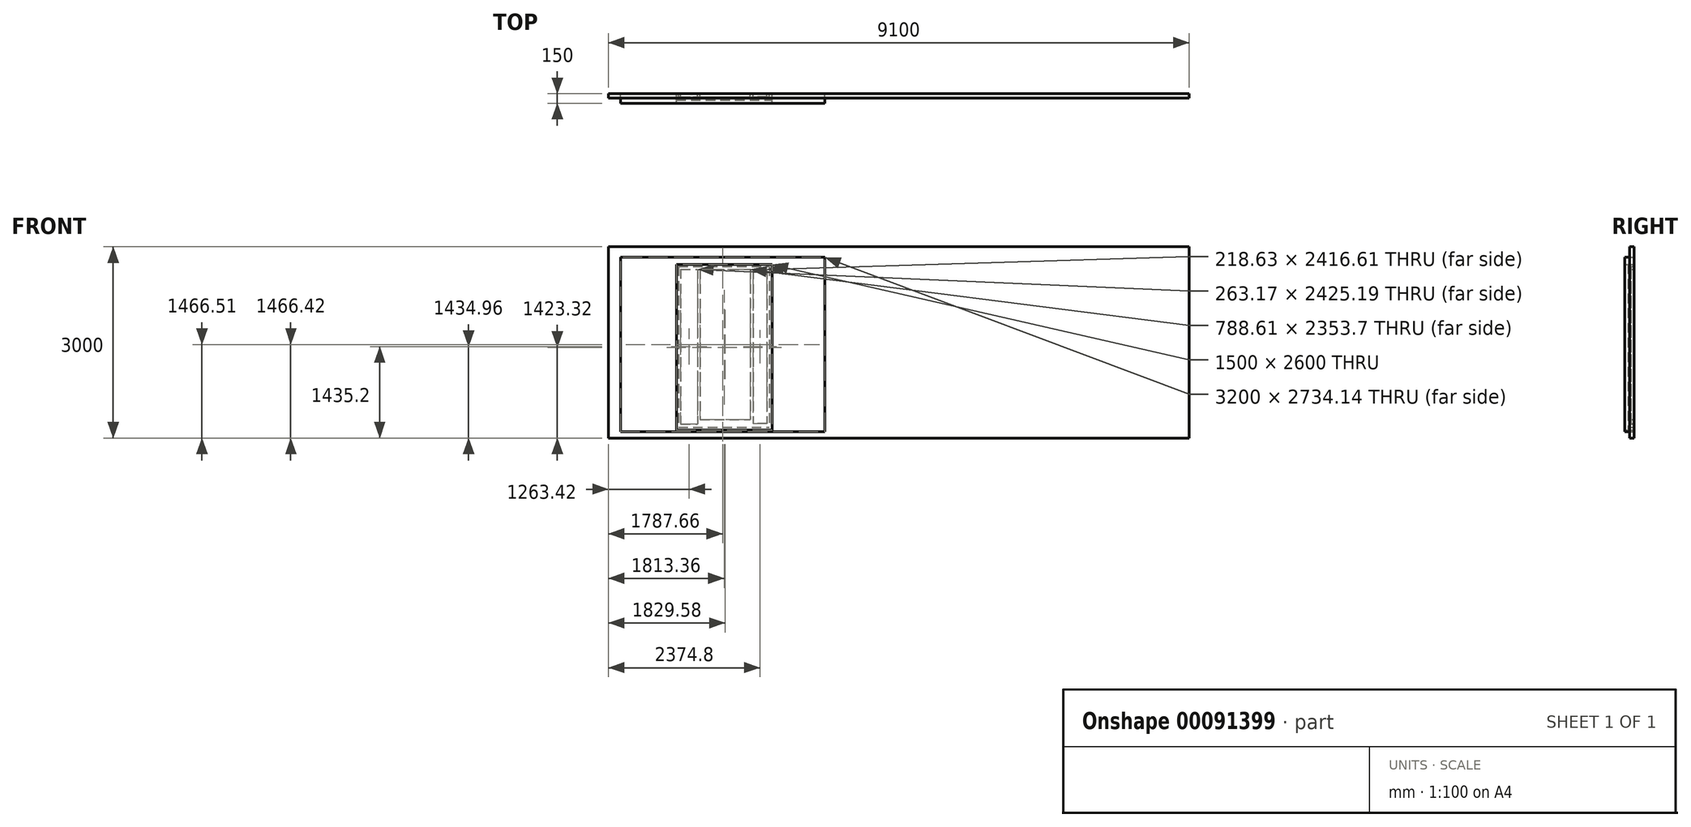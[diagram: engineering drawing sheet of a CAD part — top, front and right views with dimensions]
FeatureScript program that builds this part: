
annotation { "Feature Type Name" : "Feature", "Feature Type Description" : "" }
export const myFeature = defineFeature(function(context is Context, id is Id, definition is map)
    precondition{}
    {
        {
            var Q0;
            Q0=qCreatedBy(makeId("Front.planeOp"),FACE);
            var sketch = newSketch(context, id + "F0", { "sketchPlane" : qUnion([Q0])});
            skLineSegment(sketch, "E0.bottom", {"start": v(-2377.1, 2154.8) * mm, "end": v(6722.9, 2154.8) * mm});
            skLineSegment(sketch, "E0.top", {"start": v(-2377.1, -845.2) * mm, "end": v(6722.9, -845.2) * mm});
            skLineSegment(sketch, "E0.left", {"start": v(-2377.1, 2154.8) * mm, "end": v(-2377.1, -845.2) * mm});
            skLineSegment(sketch, "E0.right", {"start": v(6722.9, 2154.8) * mm, "end": v(6722.9, -845.2) * mm});
            skLineSegment(sketch, "E1.bottom", {"start": v(-2189.44, -745.77) * mm, "end": v(1010.56, -745.77) * mm});
            skLineSegment(sketch, "E1.top", {"start": v(-2189.44, 1988.37) * mm, "end": v(1010.56, 1988.37) * mm});
            skLineSegment(sketch, "E1.left", {"start": v(-2189.44, -745.77) * mm, "end": v(-2189.44, 1988.37) * mm});
            skLineSegment(sketch, "E1.right", {"start": v(1010.56, -745.77) * mm, "end": v(1010.56, 1988.37) * mm});
            skLineSegment(sketch, "E2.bottom", {"start": v(-1313.74, 1878.1) * mm, "end": v(186.26, 1878.1) * mm});
            skLineSegment(sketch, "E2.top", {"start": v(-1313.74, -721.9) * mm, "end": v(186.26, -721.9) * mm});
            skLineSegment(sketch, "E2.left", {"start": v(-1313.74, 1878.1) * mm, "end": v(-1313.74, -721.9) * mm});
            skLineSegment(sketch, "E2.right", {"start": v(186.26, 1878.1) * mm, "end": v(186.26, -721.9) * mm});
            skSolve(sketch);
        }
        {
            var Q0;
            Q0=makeQuery(id+"F0.imprint","IMPRINT",FACE,{"disambiguationData":[TD([[makeQuery(id+"F0.imprint","IMPRINT",EDGE,{"derivedFrom":sQuery(id+"F0.wireOp",EDGE,"E0.bottom")}),-1.0]])]});
            extrude(context, id + "F1", {"entities" : qUnion([Q0]), "depth" : 70 * mm});
        }
        {
            var Q0;
            Q0=makeQuery(id+"F0.imprint","IMPRINT",FACE,{"disambiguationData":[TD([[makeQuery(id+"F0.imprint","IMPRINT",EDGE,{"derivedFrom":sQuery(id+"F0.wireOp",EDGE,"E1.bottom")}),1.0]])]});
            extrude(context, id + "F2", {"entities" : qUnion([Q0]), "depth" : 150 * mm});
        }
        {
            var Q0;
            Q0=makeQuery(id+"F0.imprint","IMPRINT",FACE,{"disambiguationData":[TD([[makeQuery(id+"F0.imprint","IMPRINT",EDGE,{"derivedFrom":sQuery(id+"F0.wireOp",EDGE,"E2.bottom")}),-1.0]])]});
            extrude(context, id + "F3", {"entities" : qUnion([Q0]), "depth" : 100 * mm});
        }
        {
            var Q0;
            Q0=qCreatedBy(makeId("Front.planeOp"),FACE);
            var sketch = newSketch(context, id + "F4", { "sketchPlane" : qUnion([Q0])});
            skLineSegment(sketch, "E3.bottom", {"start": v(-1281.54, 1846.59) * mm, "end": v(144.03, 1846.59) * mm});
            skLineSegment(sketch, "E3.top", {"start": v(-1281.54, -676.97) * mm, "end": v(144.03, -676.97) * mm});
            skLineSegment(sketch, "E3.left", {"start": v(-1281.54, 1846.59) * mm, "end": v(-1281.54, -676.97) * mm});
            skLineSegment(sketch, "E3.right", {"start": v(144.03, 1846.59) * mm, "end": v(144.03, -676.97) * mm});
            skLineSegment(sketch, "E4.bottom", {"start": v(-941.83, 1798.06) * mm, "end": v(-153.22, 1798.06) * mm});
            skLineSegment(sketch, "E4.top", {"start": v(-941.83, -555.64) * mm, "end": v(-153.22, -555.64) * mm});
            skLineSegment(sketch, "E4.left", {"start": v(-941.83, 1798.06) * mm, "end": v(-941.83, -555.64) * mm});
            skLineSegment(sketch, "E4.right", {"start": v(-153.22, 1798.06) * mm, "end": v(-153.22, -555.64) * mm});
            skLineSegment(sketch, "E5.bottom", {"start": v(-1245.26, 1802.59) * mm, "end": v(-982.1, 1802.59) * mm});
            skLineSegment(sketch, "E5.top", {"start": v(-1245.26, -622.6) * mm, "end": v(-982.1, -622.6) * mm});
            skLineSegment(sketch, "E5.left", {"start": v(-1245.26, 1802.59) * mm, "end": v(-1245.26, -622.6) * mm});
            skLineSegment(sketch, "E5.right", {"start": v(-982.1, 1802.59) * mm, "end": v(-982.1, -622.6) * mm});
            skLineSegment(sketch, "E6.bottom", {"start": v(107.01, 1798.06) * mm, "end": v(-111.62, 1798.06) * mm});
            skLineSegment(sketch, "E6.top", {"start": v(107.01, -618.55) * mm, "end": v(-111.62, -618.55) * mm});
            skLineSegment(sketch, "E6.left", {"start": v(107.01, 1798.06) * mm, "end": v(107.01, -618.55) * mm});
            skLineSegment(sketch, "E6.right", {"start": v(-111.62, 1798.06) * mm, "end": v(-111.62, -618.55) * mm});
            skLineSegment(sketch, "E7.bottom", {"start": v(-1245.26, 806.6) * mm, "end": v(-982.1, 806.6) * mm});
            skLineSegment(sketch, "E7.top", {"start": v(-1245.26, 478.65) * mm, "end": v(-982.1, 478.65) * mm});
            skLineSegment(sketch, "E7.left", {"start": v(-1245.26, 806.6) * mm, "end": v(-1245.26, 478.65) * mm});
            skLineSegment(sketch, "E7.right", {"start": v(-982.1, 806.6) * mm, "end": v(-982.1, 478.65) * mm});
            skLineSegment(sketch, "E8.bottom", {"start": v(-111.62, 851.14) * mm, "end": v(107.01, 851.14) * mm});
            skLineSegment(sketch, "E8.top", {"start": v(-111.62, 470.55) * mm, "end": v(107.01, 470.55) * mm});
            skLineSegment(sketch, "E8.left", {"start": v(-111.62, 851.14) * mm, "end": v(-111.62, 470.55) * mm});
            skLineSegment(sketch, "E8.right", {"start": v(107.01, 851.14) * mm, "end": v(107.01, 470.55) * mm});
            skSolve(sketch);
        }
        {
            var Q0;
            Q0 = qSketchRegion(id + "F4", true);
            extrude(context, id + "F5", {"entities" : qUnion([Q0]), "depth" : 50 * mm});
        }
    });
